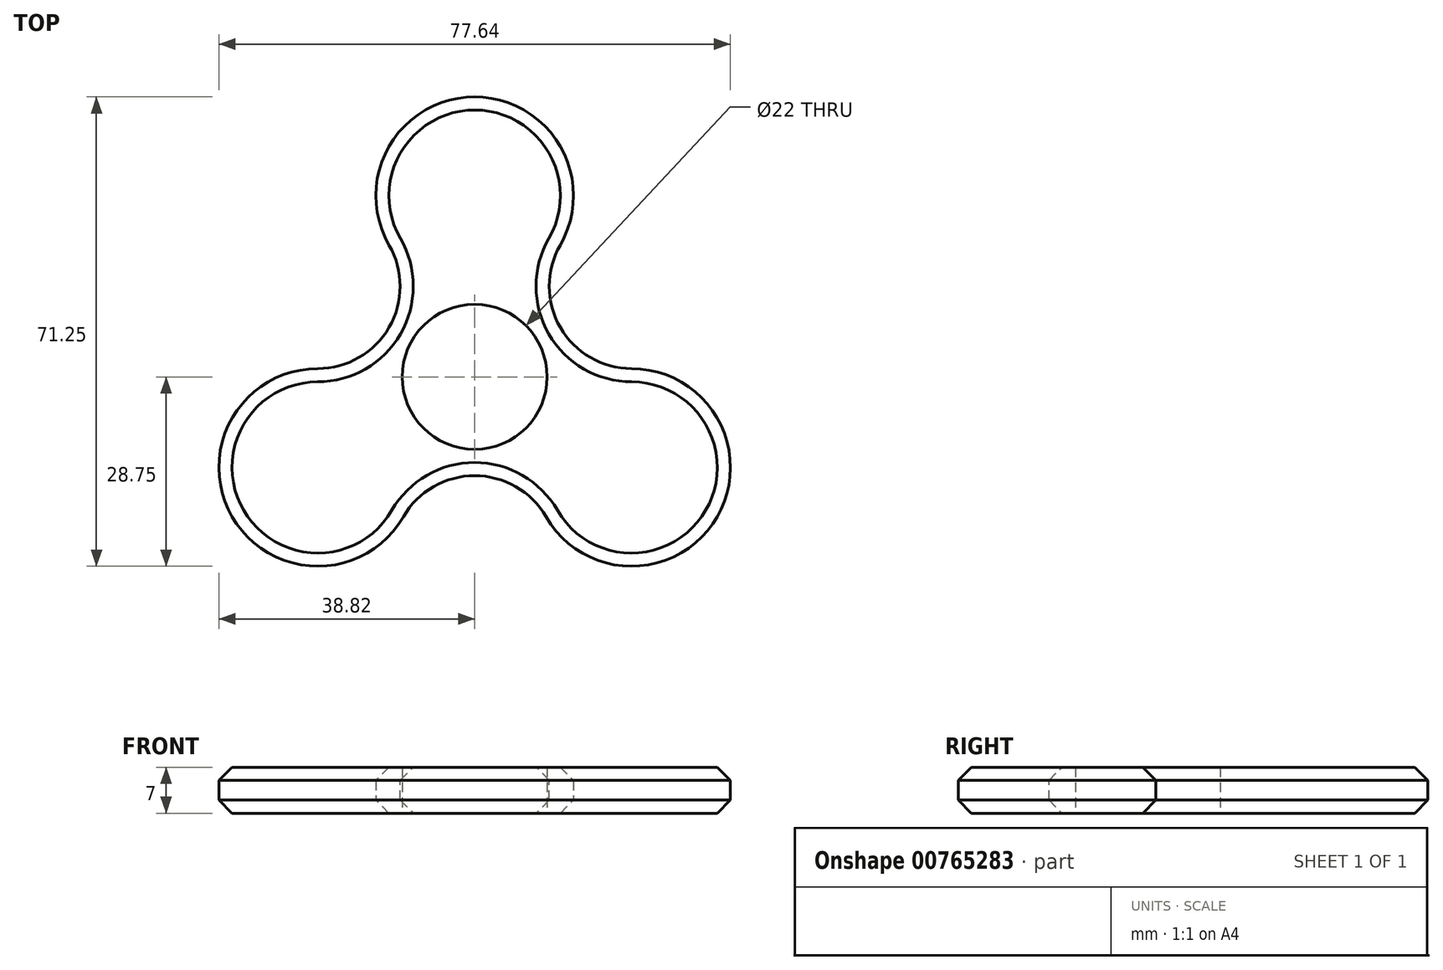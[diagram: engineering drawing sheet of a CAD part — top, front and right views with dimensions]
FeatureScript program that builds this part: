
annotation { "Feature Type Name" : "Feature", "Feature Type Description" : "" }
export const myFeature = defineFeature(function(context is Context, id is Id, definition is map)
    precondition{}
    {
        {
            var Q0;
            Q0=qCreatedBy(makeId("Top.planeOp"),FACE);
            var sketch = newSketch(context, id + "F0", { "sketchPlane" : qUnion([Q0])});
            skCircle(sketch, "E0", {"center": v(0, 0) * mm, "radius": 11 * mm});
            skLineSegment(sketch, "E1", {"start": v(0, 0) * mm, "end": v(0, 27.5) * mm, "construction": true});
            skCircle(sketch, "E2", {"center": v(0, 0) * mm, "radius": 15 * mm});
            skCircle(sketch, "E3", {"center": v(0, 27.5) * mm, "radius": 15 * mm});
            skCircle(sketch, "E4.1.0", {"center": v(-23.82, -13.75) * mm, "radius": 15 * mm});
            skCircle(sketch, "E4.2.0", {"center": v(23.82, -13.75) * mm, "radius": 15 * mm});
            skSolve(sketch);
        }
        {
            var Q0;
            Q0=qSketchRegion(id+"F0",true);
            extrude(context, id + "F1", {"entities" : qUnion([Q0]), "depth" : 7 * mm, "offsetDistance" : 25 * mm});
        }
        {
            var Q0;
            {var subQ0=sQuery(id+"F0.wireOp",EDGE,"E3");var subQ1=sQuery(id+"F0.wireOp",EDGE,"E2");Q0=makeQuery(id+"F1.opExtrude","SWEPT_EDGE",EDGE,{"disambiguationData":[OSD([subQ1,subQ0]),TDD([makeQuery(id+"F0.imprint","INTERSECT",VERTEX,{"disambiguationData":[OD(1.0)],"derivedFrom":[subQ1,subQ0]})])]});}
            var Q1;
            {var subQ0=sQuery(id+"F0.wireOp",EDGE,"E4.2.0");var subQ1=sQuery(id+"F0.wireOp",EDGE,"E2");Q1=makeQuery(id+"F1.opExtrude","SWEPT_EDGE",EDGE,{"disambiguationData":[OSD([subQ1,subQ0]),TDD([makeQuery(id+"F0.imprint","INTERSECT",VERTEX,{"disambiguationData":[OD(1.0)],"derivedFrom":[subQ1,subQ0]})])]});}
            var Q2;
            {var subQ0=sQuery(id+"F0.wireOp",EDGE,"E4.1.0");var subQ1=sQuery(id+"F0.wireOp",EDGE,"E2");Q2=makeQuery(id+"F1.opExtrude","SWEPT_EDGE",EDGE,{"disambiguationData":[OSD([subQ1,subQ0]),TDD([makeQuery(id+"F0.imprint","INTERSECT",VERTEX,{"disambiguationData":[OD(0.0)],"derivedFrom":[subQ1,subQ0]})])]});}
            var Q3;
            {var subQ0=sQuery(id+"F0.wireOp",EDGE,"E3");var subQ1=sQuery(id+"F0.wireOp",EDGE,"E2");Q3=makeQuery(id+"F1.opExtrude","SWEPT_EDGE",EDGE,{"disambiguationData":[OSD([subQ1,subQ0]),TDD([makeQuery(id+"F0.imprint","INTERSECT",VERTEX,{"disambiguationData":[OD(0.0)],"derivedFrom":[subQ1,subQ0]})])]});}
            var Q4;
            {var subQ0=sQuery(id+"F0.wireOp",EDGE,"E4.1.0");var subQ1=sQuery(id+"F0.wireOp",EDGE,"E2");Q4=makeQuery(id+"F1.opExtrude","SWEPT_EDGE",EDGE,{"disambiguationData":[OSD([subQ1,subQ0]),TDD([makeQuery(id+"F0.imprint","INTERSECT",VERTEX,{"disambiguationData":[OD(1.0)],"derivedFrom":[subQ1,subQ0]})])]});}
            var Q5;
            {var subQ0=sQuery(id+"F0.wireOp",EDGE,"E4.2.0");var subQ1=sQuery(id+"F0.wireOp",EDGE,"E2");Q5=makeQuery(id+"F1.opExtrude","SWEPT_EDGE",EDGE,{"disambiguationData":[OSD([subQ1,subQ0]),TDD([makeQuery(id+"F0.imprint","INTERSECT",VERTEX,{"disambiguationData":[OD(0.0)],"derivedFrom":[subQ1,subQ0]})])]});}
            fillet(context, id + "F2", {"entities" : qUnion([Q0, Q1, Q2, Q3, Q4, Q5]), "radius" : 12.5 * mm, "tangentPropagation" : true, "allowEdgeOverflow" : false});
        }
        {
            var Q0;
            {var subQ0=sQuery(id+"F0.wireOp",EDGE,"E4.1.0");var subQ1=sQuery(id+"F0.wireOp",EDGE,"E2");Q0=makeQuery(id+"F2.opFillet","BLEND_EDGE",EDGE,{"blendedFrom":[makeQuery(id+"F1.opExtrude","SWEPT_EDGE",EDGE,{"disambiguationData":[OSD([subQ1,subQ0]),TDD([makeQuery(id+"F0.imprint","INTERSECT",VERTEX,{"disambiguationData":[OD(1.0)],"derivedFrom":[subQ1,subQ0]})])]}),makeQuery(id+"F1.opExtrude","CAP_FACE",FACE,{"disambiguationData":[OSD([sQuery(id+"F0.wireOp",EDGE,"E0"),sQuery(id+"F0.wireOp",EDGE,"tqlmx8ec-Aq0u-wFNW-i4RI-rEMeCH0LbpHe"),sQuery(id+"F0.wireOp",EDGE,"1547efce-2ffd-4e4f-ab09-5fdc000c0d9e.1.0"),sQuery(id+"F0.wireOp",EDGE,"1547efce-2ffd-4e4f-ab09-5fdc000c0d9e.2.0"),subQ1,sQuery(id+"F0.wireOp",EDGE,"E3"),subQ0,sQuery(id+"F0.wireOp",EDGE,"E4.2.0")])],"isStart":true})],"blendedInto":[makeQuery(id+"F1.opExtrude","CAP_FACE",FACE,{"disambiguationData":[OSD([sQuery(id+"F0.wireOp",EDGE,"E0"),sQuery(id+"F0.wireOp",EDGE,"tqlmx8ec-Aq0u-wFNW-i4RI-rEMeCH0LbpHe"),sQuery(id+"F0.wireOp",EDGE,"1547efce-2ffd-4e4f-ab09-5fdc000c0d9e.1.0"),sQuery(id+"F0.wireOp",EDGE,"1547efce-2ffd-4e4f-ab09-5fdc000c0d9e.2.0"),subQ1,sQuery(id+"F0.wireOp",EDGE,"E3"),subQ0,sQuery(id+"F0.wireOp",EDGE,"E4.2.0")])],"isStart":true})]});}
            var Q1;
            {var subQ0=sQuery(id+"F0.wireOp",EDGE,"E4.1.0");var subQ1=sQuery(id+"F0.wireOp",EDGE,"E2");Q1=makeQuery(id+"F2.opFillet","BLEND_EDGE",EDGE,{"blendedFrom":[makeQuery(id+"F1.opExtrude","SWEPT_EDGE",EDGE,{"disambiguationData":[OSD([subQ1,subQ0]),TDD([makeQuery(id+"F0.imprint","INTERSECT",VERTEX,{"disambiguationData":[OD(1.0)],"derivedFrom":[subQ1,subQ0]})])]}),makeQuery(id+"F1.opExtrude","CAP_FACE",FACE,{"disambiguationData":[OSD([sQuery(id+"F0.wireOp",EDGE,"E0"),sQuery(id+"F0.wireOp",EDGE,"tqlmx8ec-Aq0u-wFNW-i4RI-rEMeCH0LbpHe"),sQuery(id+"F0.wireOp",EDGE,"1547efce-2ffd-4e4f-ab09-5fdc000c0d9e.1.0"),sQuery(id+"F0.wireOp",EDGE,"1547efce-2ffd-4e4f-ab09-5fdc000c0d9e.2.0"),subQ1,sQuery(id+"F0.wireOp",EDGE,"E3"),subQ0,sQuery(id+"F0.wireOp",EDGE,"E4.2.0")])],"isStart":false})],"blendedInto":[makeQuery(id+"F1.opExtrude","CAP_FACE",FACE,{"disambiguationData":[OSD([sQuery(id+"F0.wireOp",EDGE,"E0"),sQuery(id+"F0.wireOp",EDGE,"tqlmx8ec-Aq0u-wFNW-i4RI-rEMeCH0LbpHe"),sQuery(id+"F0.wireOp",EDGE,"1547efce-2ffd-4e4f-ab09-5fdc000c0d9e.1.0"),sQuery(id+"F0.wireOp",EDGE,"1547efce-2ffd-4e4f-ab09-5fdc000c0d9e.2.0"),subQ1,sQuery(id+"F0.wireOp",EDGE,"E3"),subQ0,sQuery(id+"F0.wireOp",EDGE,"E4.2.0")])],"isStart":false})]});}
            chamfer(context, id + "F3", {"entities" : qUnion([Q0, Q1]), "width" : 2 * mm, "tangentPropagation" : true});
        }
    });
